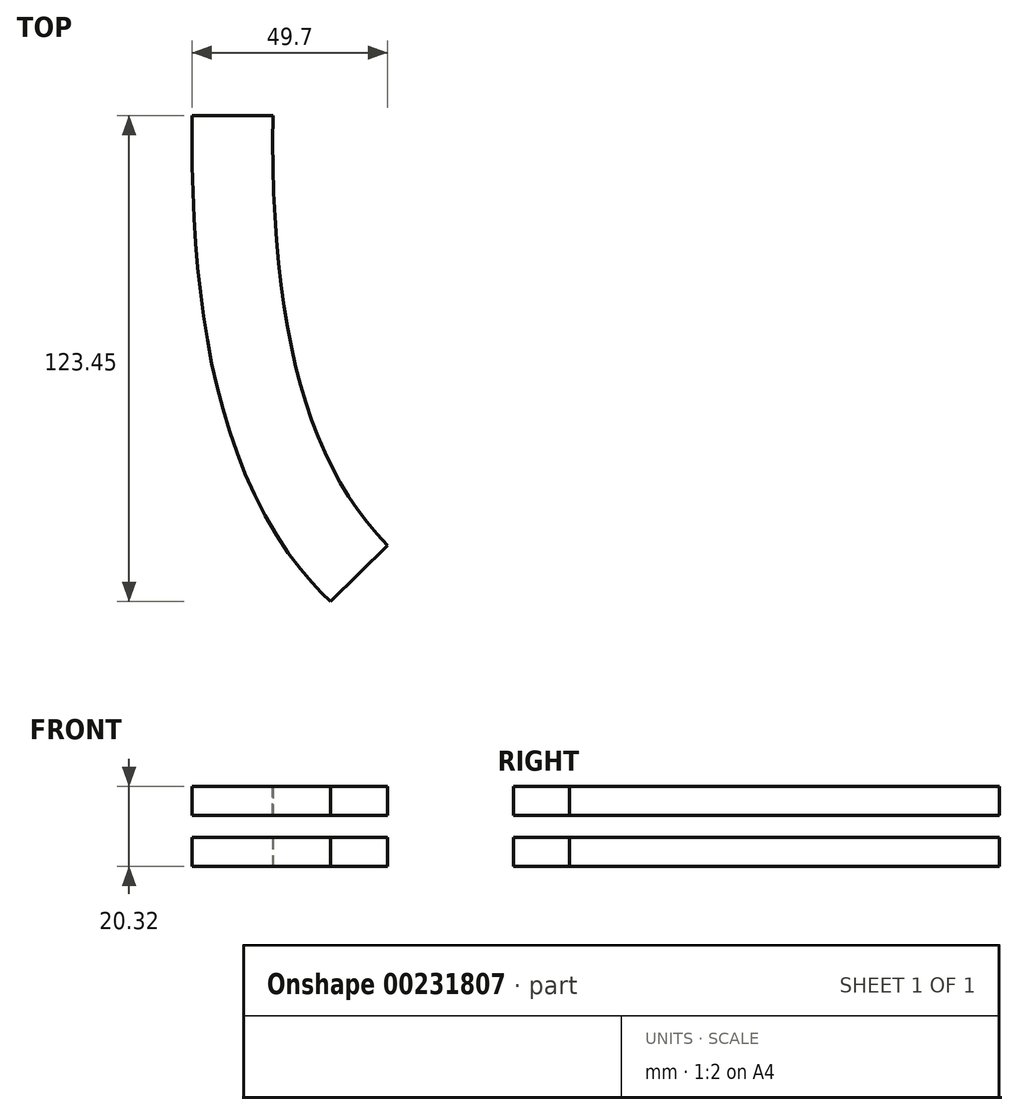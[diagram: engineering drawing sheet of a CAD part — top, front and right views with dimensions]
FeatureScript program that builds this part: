
annotation { "Feature Type Name" : "Feature", "Feature Type Description" : "" }
export const myFeature = defineFeature(function(context is Context, id is Id, definition is map)
    precondition{}
    {
        {
            var Q0;
            Q0=qCreatedBy(makeId("Top.planeOp"),FACE);
            var sketch = newSketch(context, id + "F0", { "sketchPlane" : qUnion([Q0])});
            skFitSpline(sketch, "E0", {"points": [v(-29.53, 62.81) * mm, v(-1.02, -65.9) * mm], "startDerivative": vector(-9.59, -188.43) * mm, "endDerivative": vector(70.95, -72.17) * mm});
            skFitSpline(sketch, "E1.0", {"points": [v(-54.9, 64.1) * mm, v(-55.32, 55.9) * mm, v(-55.8, 40.1) * mm, v(-55.33, 18.02) * mm, v(-53.6, -2.52) * mm, v(-50.45, -21.63) * mm, v(-45.7, -39.39) * mm, v(-39.1, -55.82) * mm, v(-30.4, -70.8) * mm, v(-23.13, -79.64) * mm, v(-19.13, -83.7) * mm]});
            skLineSegment(sketch, "E2", {"start": v(-55.57, 43.35) * mm, "end": v(-30.17, 43.35) * mm});
            skLineSegment(sketch, "E3", {"start": v(-19.18, -83.65) * mm, "end": v(-1.02, -65.9) * mm});
            skFitSpline(sketch, "E4.0", {"points": [v(-49.83, 63.84) * mm, v(-50.24, 55.72) * mm, v(-50.7, 40.06) * mm, v(-50.25, 18.27) * mm, v(-48.55, -1.9) * mm, v(-45.47, -20.58) * mm, v(-40.85, -37.8) * mm, v(-34.5, -53.6) * mm, v(-26.2, -67.9) * mm, v(-19.3, -76.3) * mm, v(-15.51, -80.14) * mm]});
            skLineSegment(sketch, "E5", {"start": v(-15.56, -80.1) * mm, "end": v(-15.55, -80.1) * mm});
            skSolve(sketch);
        }
        {
            var Q0;
            {var subQ2=sQuery(id+"F0.wireOp",EDGE,"E0");Q0=makeQuery(id+"F0.imprint","IMPRINT",FACE,{"disambiguationData":[TD([[makeQuery(id+"F0.imprint","IMPRINT",EDGE,{"derivedFrom":subQ2}),-1.0]])]});}
            var Q1;
            {var subQ2=sQuery(id+"F0.wireOp",EDGE,"E1.0");Q1=makeQuery(id+"F0.imprint","IMPRINT",FACE,{"disambiguationData":[TD([[makeQuery(id+"F0.imprint","IMPRINT",EDGE,{"derivedFrom":subQ2}),1.0]])]});}
            extrude(context, id + "F1", {"entities" : qUnion([Q0, Q1]), "endBound" : BoundingType.SYMMETRIC, "depth" : 20.32 * mm});
        }
        {
            var Q0;
            {var subQ2=sQuery(id+"F0.wireOp",EDGE,"E0");Q0=makeQuery(id+"F0.imprint","IMPRINT",FACE,{"disambiguationData":[TD([[makeQuery(id+"F0.imprint","IMPRINT",EDGE,{"derivedFrom":subQ2}),-1.0]])]});}
            extrude(context, id + "F2", {"entities" : qUnion([Q0]), "operationType" : NewBodyOperationType.REMOVE, "endBound" : BoundingType.SYMMETRIC, "oppositeDirection" : true, "depth" : 5.6 * mm});
        }
    });
